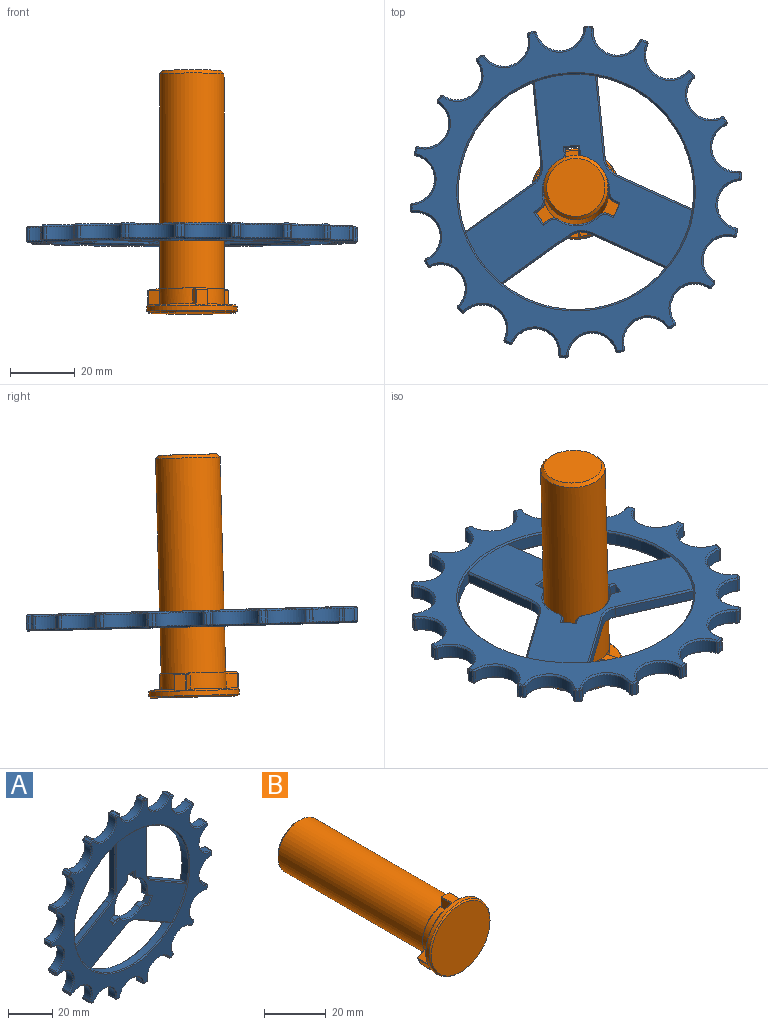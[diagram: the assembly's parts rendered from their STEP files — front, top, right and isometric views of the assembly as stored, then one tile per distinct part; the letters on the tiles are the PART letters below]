
ASSEMBLY  parts=2 mates=1
PART A: 305 faces, bbox 102.8x5x101.5 mm
  f0: cylinder r=36.4mm len=44.48mm, axis (0,1,0), area 224.4mm2, adj f94,f96,f123,f125,f153,f155,f303,f304
  f1: cylinder r=36.4mm len=44.48mm, axis (0,1,0), area 224.4mm2, adj f91,f93,f126,f128,f150,f152,f303,f304
  f2: cylinder r=51.4mm len=4mm, axis (0,1,0), area 5.4mm2, adj f3,f74,f161,f233
  f3: cylinder r=0.77mm len=4mm, axis (0,1,0), area 4.8mm2, adj f2,f4,f159,f231
  f4: cylinder r=7.5mm len=12.33mm, axis (0,1,0), area 83.9mm2, adj f3,f5,f160,f232
  f5: cylinder r=0.77mm len=4mm, axis (0,1,0), area 4.8mm2, adj f4,f6,f162,f234
  f6: cylinder r=51.4mm len=4mm, axis (0,1,0), area 5.4mm2, adj f5,f7,f164,f236
  f7: cylinder r=0.77mm len=4mm, axis (0,1,0), area 4.8mm2, adj f6,f8,f166,f238
  f8: cylinder r=7.5mm len=13.25mm, axis (0,1,0), area 83.9mm2, adj f7,f9,f168,f240
  f9: cylinder r=0.77mm len=4mm, axis (0,1,0), area 4.8mm2, adj f8,f10,f170,f242
  f10: cylinder r=51.4mm len=4mm, axis (0,1,0), area 5.4mm2, adj f9,f11,f172,f244
  f11: cylinder r=0.77mm len=4mm, axis (0,1,0), area 4.8mm2, adj f10,f12,f174,f246
  f12: cylinder r=7.5mm len=14.55mm, axis (0,1,0), area 83.9mm2, adj f11,f13,f176,f248
  f13: cylinder r=0.77mm len=4mm, axis (0,1,0), area 4.8mm2, adj f12,f14,f178,f250
  f14: cylinder r=51.4mm len=4mm, axis (0,1,0), area 5.4mm2, adj f13,f15,f180,f252
  f15: cylinder r=0.77mm len=4mm, axis (0,1,0), area 4.8mm2, adj f14,f16,f182,f254
  f16: cylinder r=7.5mm len=14.55mm, axis (0,1,0), area 83.9mm2, adj f15,f17,f184,f256
  f17: cylinder r=0.77mm len=4mm, axis (0,1,0), area 4.8mm2, adj f16,f18,f186,f258
  f18: cylinder r=51.4mm len=4mm, axis (0,1,0), area 5.4mm2, adj f17,f19,f188,f260
  f19: cylinder r=0.77mm len=4mm, axis (0,1,0), area 4.8mm2, adj f18,f20,f190,f262
  f20: cylinder r=7.5mm len=13.25mm, axis (0,1,0), area 83.9mm2, adj f19,f21,f192,f264
  f21: cylinder r=0.77mm len=4mm, axis (0,1,0), area 4.8mm2, adj f20,f22,f194,f266
  f22: cylinder r=51.4mm len=4mm, axis (0,1,0), area 5.4mm2, adj f21,f23,f196,f268
  f23: cylinder r=0.77mm len=4mm, axis (0,1,0), area 4.8mm2, adj f22,f24,f198,f270
  f24: cylinder r=7.5mm len=12.33mm, axis (0,1,0), area 83.9mm2, adj f23,f25,f200,f272
  f25: cylinder r=0.77mm len=4mm, axis (0,1,0), area 4.8mm2, adj f24,f26,f202,f274
  f26: cylinder r=51.4mm len=4mm, axis (0,1,0), area 5.4mm2, adj f25,f27,f204,f276
  f27: cylinder r=0.77mm len=4mm, axis (0,1,0), area 4.8mm2, adj f26,f28,f206,f278
  f28: cylinder r=7.5mm len=14mm, axis (0,1,0), area 83.9mm2, adj f27,f29,f208,f280
  f29: cylinder r=0.77mm len=4mm, axis (0,1,0), area 4.8mm2, adj f28,f30,f210,f282
  f30: cylinder r=51.4mm len=4mm, axis (0,1,0), area 5.4mm2, adj f29,f31,f212,f284
  f31: cylinder r=0.77mm len=4mm, axis (0,1,0), area 4.8mm2, adj f30,f32,f214,f286
  f32: cylinder r=7.5mm len=14.78mm, axis (0,1,0), area 83.9mm2, adj f31,f33,f216,f288
  f33: cylinder r=0.77mm len=4mm, axis (0,1,0), area 4.8mm2, adj f32,f34,f218,f290
  f34: cylinder r=51.4mm len=4mm, axis (0,1,0), area 5.4mm2, adj f33,f35,f220,f292
  f35: cylinder r=0.77mm len=4mm, axis (0,1,0), area 4.8mm2, adj f34,f36,f222,f294
  f36: cylinder r=7.5mm len=14mm, axis (0,1,0), area 83.9mm2, adj f35,f37,f224,f296
  f37: cylinder r=0.77mm len=4mm, axis (0,1,0), area 4.8mm2, adj f36,f38,f226,f298
  f38: cylinder r=51.4mm len=4mm, axis (0,1,0), area 5.4mm2, adj f37,f39,f228,f300
  f39: cylinder r=0.77mm len=4mm, axis (0,1,0), area 4.8mm2, adj f38,f40,f230,f302
  f40: cylinder r=7.5mm len=12.33mm, axis (0,1,0), area 83.9mm2, adj f39,f41,f229,f301
  f41: cylinder r=0.77mm len=4mm, axis (0,1,0), area 4.8mm2, adj f40,f42,f227,f299
  f42: cylinder r=51.4mm len=4mm, axis (0,1,0), area 5.4mm2, adj f41,f43,f225,f297
  f43: cylinder r=0.77mm len=4mm, axis (0,1,0), area 4.8mm2, adj f42,f44,f223,f295
  f44: cylinder r=7.5mm len=13.25mm, axis (0,1,0), area 83.9mm2, adj f43,f45,f221,f293
  f45: cylinder r=0.77mm len=4mm, axis (0,1,0), area 4.8mm2, adj f44,f46,f219,f291
  f46: cylinder r=51.4mm len=4mm, axis (0,1,0), area 5.4mm2, adj f45,f47,f217,f289
  f47: cylinder r=0.77mm len=4mm, axis (0,1,0), area 4.8mm2, adj f46,f48,f215,f287
  f48: cylinder r=7.5mm len=14.55mm, axis (0,1,0), area 83.9mm2, adj f47,f49,f213,f285
  f49: cylinder r=0.77mm len=4mm, axis (0,1,0), area 4.8mm2, adj f48,f50,f211,f283
  f50: cylinder r=51.4mm len=4mm, axis (0,1,0), area 5.4mm2, adj f49,f51,f209,f281
  f51: cylinder r=0.77mm len=4mm, axis (0,1,0), area 4.8mm2, adj f50,f52,f207,f279
  f52: cylinder r=7.5mm len=14.55mm, axis (0,1,0), area 83.9mm2, adj f51,f53,f205,f277
  f53: cylinder r=0.77mm len=4mm, axis (0,1,0), area 4.8mm2, adj f52,f54,f203,f275
  f54: cylinder r=51.4mm len=4mm, axis (0,1,0), area 5.4mm2, adj f53,f55,f201,f273
  f55: cylinder r=0.77mm len=4mm, axis (0,1,0), area 4.8mm2, adj f54,f56,f199,f271
  f56: cylinder r=7.5mm len=13.25mm, axis (0,1,0), area 83.9mm2, adj f55,f57,f197,f269
  f57: cylinder r=0.77mm len=4mm, axis (0,1,0), area 4.8mm2, adj f56,f58,f195,f267
  f58: cylinder r=51.4mm len=4mm, axis (0,1,0), area 5.4mm2, adj f57,f59,f193,f265
  f59: cylinder r=0.77mm len=4mm, axis (0,1,0), area 4.8mm2, adj f58,f60,f191,f263
  f60: cylinder r=7.5mm len=12.33mm, axis (0,1,0), area 83.9mm2, adj f59,f61,f189,f261
  f61: cylinder r=0.77mm len=4mm, axis (0,1,0), area 4.8mm2, adj f60,f62,f187,f259
  f62: cylinder r=51.4mm len=4mm, axis (0,1,0), area 5.4mm2, adj f61,f63,f185,f257
  f63: cylinder r=0.77mm len=4mm, axis (0,1,0), area 4.8mm2, adj f62,f64,f183,f255
  f64: cylinder r=7.5mm len=14mm, axis (0,1,0), area 83.9mm2, adj f63,f65,f181,f253
  f65: cylinder r=0.77mm len=4mm, axis (0,1,0), area 4.8mm2, adj f64,f66,f179,f251
  f66: cylinder r=51.4mm len=4mm, axis (0,1,0), area 5.4mm2, adj f65,f67,f177,f249
  f67: cylinder r=0.77mm len=4mm, axis (0,1,0), area 4.8mm2, adj f66,f68,f175,f247
  f68: cylinder r=7.5mm len=14.78mm, axis (0,1,0), area 83.9mm2, adj f67,f69,f173,f245
  f69: cylinder r=0.77mm len=4mm, axis (0,1,0), area 4.8mm2, adj f68,f70,f171,f243
  f70: cylinder r=51.4mm len=4mm, axis (0,1,0), area 5.4mm2, adj f69,f71,f169,f241
  f71: cylinder r=0.77mm len=4mm, axis (0,1,0), area 4.8mm2, adj f70,f72,f167,f239
  f72: cylinder r=7.5mm len=14mm, axis (0,1,0), area 83.9mm2, adj f71,f74,f165,f237
  f73: cylinder r=36.4mm len=51.36mm, axis (0,1,0), area 224.4mm2, adj f88,f90,f129,f131,f156,f158,f303,f304
  f74: cylinder r=0.77mm len=4mm, axis (0,1,0), area 4.8mm2, adj f2,f72,f163,f235
  f75: plane 101.8x100.48mm, normal (0,-1,0), area 2254.9mm2, adj f159,f160,f161,f162,f163,f164,f165,f166
  f76: plane 101.8x100.48mm, normal (0,1,0), area 2254.9mm2, adj f231,f232,f233,f234,f235,f236,f237,f238
  f77: cylinder r=10mm len=10.52mm, axis (0,1,0), area 39.1mm2, adj f100,f105,f108,f145
  f78: plane 3x1.8mm, normal (1,0,0), area 5.4mm2, adj f79,f100,f106,f149
  f79: plane 5x3.5mm, normal (0,0,-1), area 14.2mm2, adj f78,f80,f99,f106,f114,f148
  f80: plane 3x1.8mm, normal (-1,0,0), area 5.4mm2, adj f79,f101,f114,f146
  f81: cylinder r=10mm len=10.52mm, axis (0,1,0), area 39.1mm2, adj f101,f102,f118,f142
  f82: plane 3x1.56mm, normal (-0.5,0,-0.87), area 5.4mm2, adj f83,f102,f122,f138
  f83: plane 3.46x3mm, normal (-0.87,0,0.5), area 12mm2, adj f82,f84,f121,f136
  f84: plane 3x1.56mm, normal (0.5,0,0.87), area 5.4mm2, adj f83,f103,f119,f134
  f85: cylinder r=10mm len=12.14mm, axis (0,1,0), area 39.1mm2, adj f103,f104,f115,f133
  f86: plane 3x1.56mm, normal (-0.5,0,0.87), area 5.4mm2, adj f87,f104,f112,f137
  f87: plane 3.46x3mm, normal (0.87,0,0.5), area 12mm2, adj f86,f97,f111,f139
  f88: plane 22.13x12.78mm, normal (0.5,0,-0.87), area 76.7mm2, adj f73,f89,f131,f158
  f89: cylinder r=6.35mm len=6.35mm, axis (0,1,0), area 19.9mm2, adj f88,f90,f130,f157
  f90: plane 22.13x12.78mm, normal (-0.5,0,-0.87), area 76.7mm2, adj f73,f89,f129,f156
  f91: plane 22.13x12.78mm, normal (0.5,0,0.87), area 76.7mm2, adj f1,f92,f128,f150
  f92: cylinder r=6.35mm len=5.5mm, axis (0,1,0), area 19.9mm2, adj f91,f93,f127,f151
  f93: plane 25.56x3mm, normal (1,0,0), area 76.7mm2, adj f1,f92,f126,f152
  f94: plane 25.56x3mm, normal (-1,0,0), area 76.7mm2, adj f0,f95,f123,f153
  f95: cylinder r=6.35mm len=5.5mm, axis (0,1,0), area 19.9mm2, adj f94,f96,f124,f154
  f96: plane 22.13x12.78mm, normal (-0.5,0,0.87), area 76.7mm2, adj f0,f95,f125,f155
  f97: plane 3x1.56mm, normal (0.5,0,-0.87), area 5.4mm2, adj f87,f105,f110,f141
  f98: plane 70.36x62.19mm, normal (0,-1,0), area 1493.9mm2, adj f132,f133,f134,f135,f136,f137,f138,f139
  f99: plane 70.36x62.19mm, normal (0,1,0), area 1496.4mm2, adj f79,f106,f107,f108,f109,f110,f111,f112
  f100: cylinder r=3mm len=3mm, axis (0,1,0), area 10.6mm2, adj f77,f78,f107,f147
  f101: cylinder r=3mm len=3mm, axis (0,1,0), area 10.6mm2, adj f80,f81,f116,f144
  f102: cylinder r=3mm len=3mm, axis (0,1,0), area 10.6mm2, adj f81,f82,f120,f140
  f103: cylinder r=3mm len=3.32mm, axis (0,1,0), area 10.6mm2, adj f84,f85,f117,f132
  f104: cylinder r=3mm len=3.32mm, axis (0,1,0), area 10.6mm2, adj f85,f86,f113,f135
  f105: cylinder r=3mm len=3mm, axis (0,1,0), area 10.6mm2, adj f77,f97,f109,f143
  f106: plane 1.8x0.5mm, normal (0.71,0.71,0), area 1.3mm2, adj f78,f79,f99,f107
  f107: cone r=2.5mm half-angle=45deg, axis (0,-1,0), area 2.3mm2, adj f99,f100,f106,f108
  f108: cone r=10.5mm half-angle=45deg, axis (0,1,0), area 9.5mm2, adj f77,f99,f107,f109
  f109: cone r=2.5mm half-angle=45deg, axis (0,-1,0), area 2.3mm2, adj f99,f105,f108,f110
  f110: plane 2.24x1.33mm, normal (0.35,0.71,-0.61), area 1.4mm2, adj f97,f99,f109,f111
  f111: plane 4.33x2.68mm, normal (0.61,0.71,0.35), area 3.2mm2, adj f87,f99,f110,f112
  f112: plane 1.99x1.58mm, normal (-0.35,0.71,0.61), area 1.4mm2, adj f86,f99,f111,f113
  f113: cone r=2.5mm half-angle=45deg, axis (0,-1,0), area 2.3mm2, adj f99,f104,f112,f115
  f114: plane 1.8x0.5mm, normal (-0.71,0.71,0), area 1.3mm2, adj f79,f80,f99,f116
  f115: cone r=10.5mm half-angle=45deg, axis (0,1,0), area 9.5mm2, adj f85,f99,f113,f117
  f116: cone r=2.5mm half-angle=45deg, axis (0,-1,0), area 2.3mm2, adj f99,f101,f114,f118
  f117: cone r=2.5mm half-angle=45deg, axis (0,-1,0), area 2.3mm2, adj f99,f103,f115,f119
  f118: cone r=10.5mm half-angle=45deg, axis (0,1,0), area 9.5mm2, adj f81,f99,f116,f120
  f119: plane 1.99x1.58mm, normal (0.35,0.71,0.61), area 1.4mm2, adj f84,f99,f117,f121
  f120: cone r=2.5mm half-angle=45deg, axis (0,-1,0), area 2.3mm2, adj f99,f102,f118,f122
  f121: plane 4.33x2.68mm, normal (-0.61,0.71,0.35), area 3.2mm2, adj f83,f99,f119,f122
  f122: plane 2.24x1.33mm, normal (-0.35,0.71,-0.61), area 1.4mm2, adj f82,f99,f120,f121
  f123: plane 25.7x0.5mm, normal (-0.71,0.71,0), area 18.1mm2, adj f0,f94,f99,f124
  f124: cone r=6.85mm half-angle=45deg, axis (0,1,0), area 4.9mm2, adj f95,f99,f123,f125
  f125: plane 22.38x13.28mm, normal (-0.35,0.71,0.61), area 18.1mm2, adj f0,f96,f99,f124
  f126: plane 25.7x0.5mm, normal (0.71,0.71,0), area 18.1mm2, adj f1,f93,f99,f127
  f127: cone r=6.85mm half-angle=45deg, axis (0,1,0), area 4.9mm2, adj f92,f99,f126,f128
  f128: plane 22.38x13.28mm, normal (0.35,0.71,0.61), area 18.1mm2, adj f1,f91,f99,f127
  f129: plane 22.5x13.21mm, normal (-0.35,0.71,-0.61), area 18.1mm2, adj f73,f90,f99,f130
  f130: cone r=6.85mm half-angle=45deg, axis (0,1,0), area 4.9mm2, adj f89,f99,f129,f131
  f131: plane 22.5x13.21mm, normal (0.35,0.71,-0.61), area 18.1mm2, adj f73,f88,f99,f130
  f132: cone r=2.5mm half-angle=45deg, axis (0,1,0), area 2.3mm2, adj f98,f103,f133,f134
  f133: cone r=10mm half-angle=45deg, axis (0,-1,0), area 9.5mm2, adj f85,f98,f132,f135
  f134: plane 1.99x1.58mm, normal (0.35,-0.71,0.61), area 1.4mm2, adj f84,f98,f132,f136
  f135: cone r=2.5mm half-angle=45deg, axis (0,1,0), area 2.3mm2, adj f98,f104,f133,f137
  f136: plane 4.33x2.68mm, normal (-0.61,-0.71,0.35), area 3.2mm2, adj f83,f98,f134,f138
  f137: plane 1.99x1.58mm, normal (-0.35,-0.71,0.61), area 1.4mm2, adj f86,f98,f135,f139
  f138: plane 2.24x1.33mm, normal (-0.35,-0.71,-0.61), area 1.4mm2, adj f82,f98,f136,f140
  f139: plane 4.33x2.68mm, normal (0.61,-0.71,0.35), area 3.2mm2, adj f87,f98,f137,f141
  f140: cone r=2.5mm half-angle=45deg, axis (0,1,0), area 2.3mm2, adj f98,f102,f138,f142
  f141: plane 2.24x1.33mm, normal (0.35,-0.71,-0.61), area 1.4mm2, adj f97,f98,f139,f143
  f142: cone r=10mm half-angle=45deg, axis (0,-1,0), area 9.5mm2, adj f81,f98,f140,f144
  f143: cone r=2.5mm half-angle=45deg, axis (0,1,0), area 2.3mm2, adj f98,f105,f141,f145
  f144: cone r=2.5mm half-angle=45deg, axis (0,1,0), area 2.3mm2, adj f98,f101,f142,f146
  f145: cone r=10mm half-angle=45deg, axis (0,-1,0), area 9.5mm2, adj f77,f98,f143,f147
  f146: plane 2.3x0.5mm, normal (-0.71,-0.71,0), area 1.4mm2, adj f80,f98,f144,f148
  f147: cone r=2.5mm half-angle=45deg, axis (0,1,0), area 2.3mm2, adj f98,f100,f145,f149
  f148: plane 5x0.5mm, normal (0,-0.71,-0.71), area 3.2mm2, adj f79,f98,f146,f149
  f149: plane 2.3x0.5mm, normal (0.71,-0.71,0), area 1.4mm2, adj f78,f98,f147,f148
  f150: plane 22.38x13.28mm, normal (0.35,-0.71,0.61), area 18.1mm2, adj f1,f91,f98,f151
  f151: cone r=6.35mm half-angle=45deg, axis (0,-1,0), area 4.9mm2, adj f92,f98,f150,f152
  f152: plane 25.7x0.5mm, normal (0.71,-0.71,0), area 18.1mm2, adj f1,f93,f98,f151
  f153: plane 25.7x0.5mm, normal (-0.71,-0.71,0), area 18.1mm2, adj f0,f94,f98,f154
  f154: cone r=6.35mm half-angle=45deg, axis (0,-1,0), area 4.9mm2, adj f95,f98,f153,f155
  f155: plane 22.38x13.28mm, normal (-0.35,-0.71,0.61), area 18.1mm2, adj f0,f96,f98,f154
  f156: plane 22.5x13.21mm, normal (-0.35,-0.71,-0.61), area 18.1mm2, adj f73,f90,f98,f157
  f157: cone r=6.35mm half-angle=45deg, axis (0,-1,0), area 4.9mm2, adj f89,f98,f156,f158
  f158: plane 22.5x13.21mm, normal (0.35,-0.71,-0.61), area 18.1mm2, adj f73,f88,f98,f157
  f159: cone r=0.27mm half-angle=45deg, axis (0,1,0), area 0.6mm2, adj f3,f75,f160,f161
  f160: cone r=7.5mm half-angle=45deg, axis (0,-1,0), area 15.3mm2, adj f4,f75,f159,f162
  f161: cone r=50.9mm half-angle=45deg, axis (0,1,0), area 0.9mm2, adj f2,f75,f159,f163
  f162: cone r=0.27mm half-angle=45deg, axis (0,1,0), area 0.6mm2, adj f5,f75,f160,f164
  f163: cone r=0.27mm half-angle=45deg, axis (0,1,0), area 0.6mm2, adj f74,f75,f161,f165
  f164: cone r=50.9mm half-angle=45deg, axis (0,1,0), area 0.9mm2, adj f6,f75,f162,f166
  f165: cone r=7.5mm half-angle=45deg, axis (0,-1,0), area 15.3mm2, adj f72,f75,f163,f167
  f166: cone r=0.27mm half-angle=45deg, axis (0,1,0), area 0.6mm2, adj f7,f75,f164,f168
  f167: cone r=0.27mm half-angle=45deg, axis (0,1,0), area 0.6mm2, adj f71,f75,f165,f169
  f168: cone r=7.5mm half-angle=45deg, axis (0,-1,0), area 15.3mm2, adj f8,f75,f166,f170
  f169: cone r=50.9mm half-angle=45deg, axis (0,1,0), area 0.9mm2, adj f70,f75,f167,f171
  f170: cone r=0.27mm half-angle=45deg, axis (0,1,0), area 0.6mm2, adj f9,f75,f168,f172
  f171: cone r=0.27mm half-angle=45deg, axis (0,1,0), area 0.6mm2, adj f69,f75,f169,f173
  f172: cone r=50.9mm half-angle=45deg, axis (0,1,0), area 0.9mm2, adj f10,f75,f170,f174
  f173: cone r=7.5mm half-angle=45deg, axis (0,-1,0), area 15.3mm2, adj f68,f75,f171,f175
  f174: cone r=0.27mm half-angle=45deg, axis (0,1,0), area 0.6mm2, adj f11,f75,f172,f176
  f175: cone r=0.27mm half-angle=45deg, axis (0,1,0), area 0.6mm2, adj f67,f75,f173,f177
  f176: cone r=7.5mm half-angle=45deg, axis (0,-1,0), area 15.3mm2, adj f12,f75,f174,f178
  f177: cone r=50.9mm half-angle=45deg, axis (0,1,0), area 0.9mm2, adj f66,f75,f175,f179
  f178: cone r=0.27mm half-angle=45deg, axis (0,1,0), area 0.6mm2, adj f13,f75,f176,f180
  f179: cone r=0.27mm half-angle=45deg, axis (0,1,0), area 0.6mm2, adj f65,f75,f177,f181
  f180: cone r=50.9mm half-angle=45deg, axis (0,1,0), area 0.9mm2, adj f14,f75,f178,f182
  f181: cone r=7.5mm half-angle=45deg, axis (0,-1,0), area 15.3mm2, adj f64,f75,f179,f183
  f182: cone r=0.27mm half-angle=45deg, axis (0,1,0), area 0.6mm2, adj f15,f75,f180,f184
  f183: cone r=0.27mm half-angle=45deg, axis (0,1,0), area 0.6mm2, adj f63,f75,f181,f185
  f184: cone r=7.5mm half-angle=45deg, axis (0,-1,0), area 15.3mm2, adj f16,f75,f182,f186
  f185: cone r=50.9mm half-angle=45deg, axis (0,1,0), area 0.9mm2, adj f62,f75,f183,f187
  f186: cone r=0.27mm half-angle=45deg, axis (0,1,0), area 0.6mm2, adj f17,f75,f184,f188
  f187: cone r=0.27mm half-angle=45deg, axis (0,1,0), area 0.6mm2, adj f61,f75,f185,f189
  f188: cone r=50.9mm half-angle=45deg, axis (0,1,0), area 0.9mm2, adj f18,f75,f186,f190
  f189: cone r=7.5mm half-angle=45deg, axis (0,-1,0), area 15.3mm2, adj f60,f75,f187,f191
  f190: cone r=0.27mm half-angle=45deg, axis (0,1,0), area 0.6mm2, adj f19,f75,f188,f192
  f191: cone r=0.27mm half-angle=45deg, axis (0,1,0), area 0.6mm2, adj f59,f75,f189,f193
  f192: cone r=7.5mm half-angle=45deg, axis (0,-1,0), area 15.3mm2, adj f20,f75,f190,f194
  f193: cone r=50.9mm half-angle=45deg, axis (0,1,0), area 0.9mm2, adj f58,f75,f191,f195
  f194: cone r=0.27mm half-angle=45deg, axis (0,1,0), area 0.6mm2, adj f21,f75,f192,f196
  f195: cone r=0.27mm half-angle=45deg, axis (0,1,0), area 0.6mm2, adj f57,f75,f193,f197
  f196: cone r=50.9mm half-angle=45deg, axis (0,1,0), area 0.9mm2, adj f22,f75,f194,f198
  f197: cone r=7.5mm half-angle=45deg, axis (0,-1,0), area 15.3mm2, adj f56,f75,f195,f199
  f198: cone r=0.27mm half-angle=45deg, axis (0,1,0), area 0.6mm2, adj f23,f75,f196,f200
  f199: cone r=0.27mm half-angle=45deg, axis (0,1,0), area 0.6mm2, adj f55,f75,f197,f201
  f200: cone r=7.5mm half-angle=45deg, axis (0,-1,0), area 15.3mm2, adj f24,f75,f198,f202
  f201: cone r=50.9mm half-angle=45deg, axis (0,1,0), area 0.9mm2, adj f54,f75,f199,f203
  f202: cone r=0.27mm half-angle=45deg, axis (0,1,0), area 0.6mm2, adj f25,f75,f200,f204
  f203: cone r=0.27mm half-angle=45deg, axis (0,1,0), area 0.6mm2, adj f53,f75,f201,f205
  f204: cone r=50.9mm half-angle=45deg, axis (0,1,0), area 0.9mm2, adj f26,f75,f202,f206
  f205: cone r=7.5mm half-angle=45deg, axis (0,-1,0), area 15.3mm2, adj f52,f75,f203,f207
  f206: cone r=0.27mm half-angle=45deg, axis (0,1,0), area 0.6mm2, adj f27,f75,f204,f208
  f207: cone r=0.27mm half-angle=45deg, axis (0,1,0), area 0.6mm2, adj f51,f75,f205,f209
  f208: cone r=7.5mm half-angle=45deg, axis (0,-1,0), area 15.3mm2, adj f28,f75,f206,f210
  f209: cone r=50.9mm half-angle=45deg, axis (0,1,0), area 0.9mm2, adj f50,f75,f207,f211
  f210: cone r=0.27mm half-angle=45deg, axis (0,1,0), area 0.6mm2, adj f29,f75,f208,f212
  f211: cone r=0.27mm half-angle=45deg, axis (0,1,0), area 0.6mm2, adj f49,f75,f209,f213
  f212: cone r=50.9mm half-angle=45deg, axis (0,1,0), area 0.9mm2, adj f30,f75,f210,f214
  f213: cone r=7.5mm half-angle=45deg, axis (0,-1,0), area 15.3mm2, adj f48,f75,f211,f215
  f214: cone r=0.27mm half-angle=45deg, axis (0,1,0), area 0.6mm2, adj f31,f75,f212,f216
  f215: cone r=0.27mm half-angle=45deg, axis (0,1,0), area 0.6mm2, adj f47,f75,f213,f217
  f216: cone r=7.5mm half-angle=45deg, axis (0,-1,0), area 15.3mm2, adj f32,f75,f214,f218
  f217: cone r=50.9mm half-angle=45deg, axis (0,1,0), area 0.9mm2, adj f46,f75,f215,f219
  f218: cone r=0.27mm half-angle=45deg, axis (0,1,0), area 0.6mm2, adj f33,f75,f216,f220
  f219: cone r=0.27mm half-angle=45deg, axis (0,1,0), area 0.6mm2, adj f45,f75,f217,f221
  f220: cone r=50.9mm half-angle=45deg, axis (0,1,0), area 0.9mm2, adj f34,f75,f218,f222
  f221: cone r=7.5mm half-angle=45deg, axis (0,-1,0), area 15.3mm2, adj f44,f75,f219,f223
  f222: cone r=0.27mm half-angle=45deg, axis (0,1,0), area 0.6mm2, adj f35,f75,f220,f224
  f223: cone r=0.27mm half-angle=45deg, axis (0,1,0), area 0.6mm2, adj f43,f75,f221,f225
  f224: cone r=7.5mm half-angle=45deg, axis (0,-1,0), area 15.3mm2, adj f36,f75,f222,f226
  f225: cone r=50.9mm half-angle=45deg, axis (0,1,0), area 0.9mm2, adj f42,f75,f223,f227
  f226: cone r=0.27mm half-angle=45deg, axis (0,1,0), area 0.6mm2, adj f37,f75,f224,f228
  f227: cone r=0.27mm half-angle=45deg, axis (0,1,0), area 0.6mm2, adj f41,f75,f225,f229
  f228: cone r=50.9mm half-angle=45deg, axis (0,1,0), area 0.9mm2, adj f38,f75,f226,f230
  f229: cone r=7.5mm half-angle=45deg, axis (0,-1,0), area 15.3mm2, adj f40,f75,f227,f230
  f230: cone r=0.27mm half-angle=45deg, axis (0,1,0), area 0.6mm2, adj f39,f75,f228,f229
  f231: cone r=0.77mm half-angle=45deg, axis (0,-1,0), area 0.6mm2, adj f3,f76,f232,f233
  f232: cone r=8mm half-angle=45deg, axis (0,1,0), area 15.3mm2, adj f4,f76,f231,f234
  f233: cone r=51.4mm half-angle=45deg, axis (0,-1,0), area 0.9mm2, adj f2,f76,f231,f235
  f234: cone r=0.77mm half-angle=45deg, axis (0,-1,0), area 0.6mm2, adj f5,f76,f232,f236
  f235: cone r=0.77mm half-angle=45deg, axis (0,-1,0), area 0.6mm2, adj f74,f76,f233,f237
  f236: cone r=51.4mm half-angle=45deg, axis (0,-1,0), area 0.9mm2, adj f6,f76,f234,f238
  f237: cone r=8mm half-angle=45deg, axis (0,1,0), area 15.3mm2, adj f72,f76,f235,f239
  f238: cone r=0.77mm half-angle=45deg, axis (0,-1,0), area 0.6mm2, adj f7,f76,f236,f240
  f239: cone r=0.77mm half-angle=45deg, axis (0,-1,0), area 0.6mm2, adj f71,f76,f237,f241
  f240: cone r=8mm half-angle=45deg, axis (0,1,0), area 15.3mm2, adj f8,f76,f238,f242
  f241: cone r=51.4mm half-angle=45deg, axis (0,-1,0), area 0.9mm2, adj f70,f76,f239,f243
  f242: cone r=0.77mm half-angle=45deg, axis (0,-1,0), area 0.6mm2, adj f9,f76,f240,f244
  f243: cone r=0.77mm half-angle=45deg, axis (0,-1,0), area 0.6mm2, adj f69,f76,f241,f245
  f244: cone r=51.4mm half-angle=45deg, axis (0,-1,0), area 0.9mm2, adj f10,f76,f242,f246
  f245: cone r=8mm half-angle=45deg, axis (0,1,0), area 15.3mm2, adj f68,f76,f243,f247
  f246: cone r=0.77mm half-angle=45deg, axis (0,-1,0), area 0.6mm2, adj f11,f76,f244,f248
  f247: cone r=0.77mm half-angle=45deg, axis (0,-1,0), area 0.6mm2, adj f67,f76,f245,f249
  f248: cone r=8mm half-angle=45deg, axis (0,1,0), area 15.3mm2, adj f12,f76,f246,f250
  f249: cone r=51.4mm half-angle=45deg, axis (0,-1,0), area 0.9mm2, adj f66,f76,f247,f251
  f250: cone r=0.77mm half-angle=45deg, axis (0,-1,0), area 0.6mm2, adj f13,f76,f248,f252
  f251: cone r=0.77mm half-angle=45deg, axis (0,-1,0), area 0.6mm2, adj f65,f76,f249,f253
  f252: cone r=51.4mm half-angle=45deg, axis (0,-1,0), area 0.9mm2, adj f14,f76,f250,f254
  f253: cone r=8mm half-angle=45deg, axis (0,1,0), area 15.3mm2, adj f64,f76,f251,f255
  f254: cone r=0.77mm half-angle=45deg, axis (0,-1,0), area 0.6mm2, adj f15,f76,f252,f256
  f255: cone r=0.77mm half-angle=45deg, axis (0,-1,0), area 0.6mm2, adj f63,f76,f253,f257
  f256: cone r=8mm half-angle=45deg, axis (0,1,0), area 15.3mm2, adj f16,f76,f254,f258
  f257: cone r=51.4mm half-angle=45deg, axis (0,-1,0), area 0.9mm2, adj f62,f76,f255,f259
  f258: cone r=0.77mm half-angle=45deg, axis (0,-1,0), area 0.6mm2, adj f17,f76,f256,f260
  f259: cone r=0.77mm half-angle=45deg, axis (0,-1,0), area 0.6mm2, adj f61,f76,f257,f261
  f260: cone r=51.4mm half-angle=45deg, axis (0,-1,0), area 0.9mm2, adj f18,f76,f258,f262
  f261: cone r=8mm half-angle=45deg, axis (0,1,0), area 15.3mm2, adj f60,f76,f259,f263
  f262: cone r=0.77mm half-angle=45deg, axis (0,-1,0), area 0.6mm2, adj f19,f76,f260,f264
  f263: cone r=0.77mm half-angle=45deg, axis (0,-1,0), area 0.6mm2, adj f59,f76,f261,f265
  f264: cone r=8mm half-angle=45deg, axis (0,1,0), area 15.3mm2, adj f20,f76,f262,f266
  f265: cone r=51.4mm half-angle=45deg, axis (0,-1,0), area 0.9mm2, adj f58,f76,f263,f267
  f266: cone r=0.77mm half-angle=45deg, axis (0,-1,0), area 0.6mm2, adj f21,f76,f264,f268
  f267: cone r=0.77mm half-angle=45deg, axis (0,-1,0), area 0.6mm2, adj f57,f76,f265,f269
  f268: cone r=51.4mm half-angle=45deg, axis (0,-1,0), area 0.9mm2, adj f22,f76,f266,f270
  f269: cone r=8mm half-angle=45deg, axis (0,1,0), area 15.3mm2, adj f56,f76,f267,f271
  f270: cone r=0.77mm half-angle=45deg, axis (0,-1,0), area 0.6mm2, adj f23,f76,f268,f272
  f271: cone r=0.77mm half-angle=45deg, axis (0,-1,0), area 0.6mm2, adj f55,f76,f269,f273
  f272: cone r=8mm half-angle=45deg, axis (0,1,0), area 15.3mm2, adj f24,f76,f270,f274
  f273: cone r=51.4mm half-angle=45deg, axis (0,-1,0), area 0.9mm2, adj f54,f76,f271,f275
  f274: cone r=0.77mm half-angle=45deg, axis (0,-1,0), area 0.6mm2, adj f25,f76,f272,f276
  f275: cone r=0.77mm half-angle=45deg, axis (0,-1,0), area 0.6mm2, adj f53,f76,f273,f277
  f276: cone r=51.4mm half-angle=45deg, axis (0,-1,0), area 0.9mm2, adj f26,f76,f274,f278
  f277: cone r=8mm half-angle=45deg, axis (0,1,0), area 15.3mm2, adj f52,f76,f275,f279
  f278: cone r=0.77mm half-angle=45deg, axis (0,-1,0), area 0.6mm2, adj f27,f76,f276,f280
  f279: cone r=0.77mm half-angle=45deg, axis (0,-1,0), area 0.6mm2, adj f51,f76,f277,f281
  f280: cone r=8mm half-angle=45deg, axis (0,1,0), area 15.3mm2, adj f28,f76,f278,f282
  f281: cone r=51.4mm half-angle=45deg, axis (0,-1,0), area 0.9mm2, adj f50,f76,f279,f283
  f282: cone r=0.77mm half-angle=45deg, axis (0,-1,0), area 0.6mm2, adj f29,f76,f280,f284
  f283: cone r=0.77mm half-angle=45deg, axis (0,-1,0), area 0.6mm2, adj f49,f76,f281,f285
  f284: cone r=51.4mm half-angle=45deg, axis (0,-1,0), area 0.9mm2, adj f30,f76,f282,f286
  f285: cone r=8mm half-angle=45deg, axis (0,1,0), area 15.3mm2, adj f48,f76,f283,f287
  f286: cone r=0.77mm half-angle=45deg, axis (0,-1,0), area 0.6mm2, adj f31,f76,f284,f288
  f287: cone r=0.77mm half-angle=45deg, axis (0,-1,0), area 0.6mm2, adj f47,f76,f285,f289
  f288: cone r=8mm half-angle=45deg, axis (0,1,0), area 15.3mm2, adj f32,f76,f286,f290
  f289: cone r=51.4mm half-angle=45deg, axis (0,-1,0), area 0.9mm2, adj f46,f76,f287,f291
  f290: cone r=0.77mm half-angle=45deg, axis (0,-1,0), area 0.6mm2, adj f33,f76,f288,f292
  f291: cone r=0.77mm half-angle=45deg, axis (0,-1,0), area 0.6mm2, adj f45,f76,f289,f293
  f292: cone r=51.4mm half-angle=45deg, axis (0,-1,0), area 0.9mm2, adj f34,f76,f290,f294
  f293: cone r=8mm half-angle=45deg, axis (0,1,0), area 15.3mm2, adj f44,f76,f291,f295
  f294: cone r=0.77mm half-angle=45deg, axis (0,-1,0), area 0.6mm2, adj f35,f76,f292,f296
  f295: cone r=0.77mm half-angle=45deg, axis (0,-1,0), area 0.6mm2, adj f43,f76,f293,f297
  f296: cone r=8mm half-angle=45deg, axis (0,1,0), area 15.3mm2, adj f36,f76,f294,f298
  f297: cone r=51.4mm half-angle=45deg, axis (0,-1,0), area 0.9mm2, adj f42,f76,f295,f299
  f298: cone r=0.77mm half-angle=45deg, axis (0,-1,0), area 0.6mm2, adj f37,f76,f296,f300
  f299: cone r=0.77mm half-angle=45deg, axis (0,-1,0), area 0.6mm2, adj f41,f76,f297,f301
  f300: cone r=51.4mm half-angle=45deg, axis (0,-1,0), area 0.9mm2, adj f38,f76,f298,f302
  f301: cone r=8mm half-angle=45deg, axis (0,1,0), area 15.3mm2, adj f40,f76,f299,f302
  f302: cone r=0.77mm half-angle=45deg, axis (0,-1,0), area 0.6mm2, adj f39,f76,f300,f301
  f303: cone r=36.9mm half-angle=45deg, axis (0,1,0), area 162.8mm2, adj f0,f1,f73,f76,f99
  f304: cone r=36.4mm half-angle=45deg, axis (0,-1,0), area 162.8mm2, adj f0,f1,f73,f75,f98
PART B: 38 faces, bbox 28x75x28 mm
  f0: plane 18.29x11.5mm, normal (0,1,0), area 72.1mm2, adj f2,f3,f4,f27
  f1: plane 18.29x11.5mm, normal (0,1,0), area 72.1mm2, adj f10,f11,f12,f27
  f2: plane 4.69x3.75mm, normal (-1,0,0), area 16.9mm2, adj f0,f3,f23,f27,f33
  f3: cylinder r=10mm len=13.53mm, axis (0,-1,0), area 84.8mm2, adj f0,f2,f4,f14,f23,f26
  f4: plane 4.69x3.25mm, normal (-0.5,0,0.87), area 16.9mm2, adj f0,f3,f26,f27,f30
  f5: plane 4.91x3.04mm, normal (-0.87,0,-0.5), area 16.9mm2, adj f25,f27,f29,f30
  f6: plane 4.69x3.25mm, normal (0.5,0,-0.87), area 16.9mm2, adj f7,f16,f24,f27,f29
  f7: cylinder r=10mm len=15.62mm, axis (0,-1,0), area 84.8mm2, adj f6,f8,f14,f16,f18,f24
  f8: plane 4.69x3.25mm, normal (-0.5,0,-0.87), area 16.9mm2, adj f7,f16,f18,f27,f32
  f9: plane 4.91x3.04mm, normal (0.87,0,-0.5), area 16.9mm2, adj f19,f27,f31,f32
  f10: plane 4.69x3.25mm, normal (0.5,0,0.87), area 16.9mm2, adj f1,f11,f20,f27,f31
  f11: cylinder r=10mm len=13.53mm, axis (0,-1,0), area 84.8mm2, adj f1,f10,f12,f14,f20,f21
  f12: plane 4.69x3.75mm, normal (1,0,0), area 16.9mm2, adj f1,f11,f21,f27,f34
  f13: plane 4.91x3.51mm, normal (0,0,1), area 16.9mm2, adj f22,f27,f33,f34
  f14: plane 24.53x23.3mm, normal (0,1,0), area 31.6mm2, adj f3,f7,f11,f18,f19,f20,f21,f22
  f15: cylinder r=14mm len=28mm, axis (0,-1,0), area 131.9mm2, adj f27,f28
  f16: plane 21.12x6.87mm, normal (0,1,0), area 72.1mm2, adj f6,f7,f8,f27
  f17: plane 27x27mm, normal (0,-1,0), area 572.6mm2, adj f28
  f18: plane 3.42x2.26mm, normal (-0.35,0.71,-0.61), area 2.6mm2, adj f7,f8,f14,f19,f32
  f19: plane 3.25x2.06mm, normal (0.61,0.71,-0.35), area 2.4mm2, adj f9,f14,f18,f20,f31,f32
  f20: plane 3.47x2.18mm, normal (0.35,0.71,0.61), area 2.6mm2, adj f10,f11,f14,f19,f31
  f21: plane 3.88x0.5mm, normal (0.71,0.71,0), area 2.6mm2, adj f11,f12,f14,f22,f34
  f22: plane 3.75x0.5mm, normal (0,0.71,0.71), area 2.4mm2, adj f13,f14,f21,f23,f33,f34
  f23: plane 3.88x0.5mm, normal (-0.71,0.71,0), area 2.6mm2, adj f2,f3,f14,f22,f33
  f24: plane 3.42x2.26mm, normal (0.35,0.71,-0.61), area 2.6mm2, adj f6,f7,f14,f25,f29
  f25: plane 3.25x2.06mm, normal (-0.61,0.71,-0.35), area 2.4mm2, adj f5,f14,f24,f26,f29,f30
  f26: plane 3.47x2.18mm, normal (-0.35,0.71,0.61), area 2.6mm2, adj f3,f4,f14,f25,f30
  f27: cone r=14mm half-angle=45deg, axis (0,-1,0), area 55.5mm2, adj f0,f1,f2,f4,f5,f6,f8,f9
  f28: cone r=13.5mm half-angle=45deg, axis (0,1,0), area 61.1mm2, adj f15,f17
  f29: plane 5.04x0.34mm, normal (-0.26,0,-0.97), area 1.7mm2, adj f5,f6,f24,f25,f27
  f30: plane 5.04x0.34mm, normal (-0.97,0,0.26), area 1.7mm2, adj f4,f5,f25,f26,f27
  f31: plane 5.04x0.34mm, normal (0.97,0,0.26), area 1.7mm2, adj f9,f10,f19,f20,f27
  f32: plane 5.04x0.34mm, normal (0.26,0,-0.97), area 1.7mm2, adj f8,f9,f18,f19,f27
  f33: plane 5.04x0.25mm, normal (-0.71,0,0.71), area 1.7mm2, adj f2,f13,f22,f23,f27
  f34: plane 5.04x0.25mm, normal (0.71,0,0.71), area 1.7mm2, adj f12,f13,f21,f22,f27
  f35: cylinder r=9.97mm len=66.5mm, axis (0,-1,0), area 4167.9mm2, adj f14,f37
  f36: plane 17.95x17.95mm, normal (0,1,0), area 253.1mm2, adj f37
  f37: cone r=9.97mm half-angle=45deg, axis (0,-1,0), area 84.2mm2, adj f35,f36
PLACE A rot(axis=(0.73,0.49,0.47),105.9deg) t=(-175.87,-25.08,67.98)mm
PLACE B rot(axis=(0.29,0.68,0.67),146.3deg) t=(-175.84,-25.65,46.24)mm
MATE cylindrical A.f85 <-> B.f11  axis (0,-0.03,-1) through (-175.87,-25.13,65.98)mm
